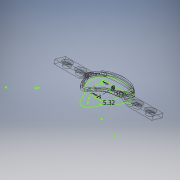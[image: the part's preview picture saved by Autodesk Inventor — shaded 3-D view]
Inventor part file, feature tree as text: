
AUTODESK INVENTOR PART (.ipt)
format: ipt  version: 2018 (Build 220112000, 112)  size: 2,541,568 bytes
history: native  units: mm
features: sketch x75, extrude x69, fillet x43, mirror x3, shell x1, hole x1
ambient origin geometry x8: Origin, YZ Plane, XZ Plane, XY Plane, X Axis, Y Axis, Z Axis, Center Point
bodies: Solid1 (feature_tree)
feature tree (192):
  extrude  "Extrusion1"  TaperAngle=0.0deg  [1 undecoded]
  extrude  "Extrusion2"  Depth=10.0mm
  extrude  "Extrusion3"  TaperAngle=0.0deg  [1 undecoded]
  shell  "Shell2"  Thickness=0.0mm
  extrude  "Extrusion4"  Depth=1.6mm
  extrude  "Extrusion6"  Depth=10.0mm TaperAngle=0.0deg
  extrude  "Extrusion7"  Depth=1.75mm
  extrude  "Extrusion8"  Depth=2.0mm
  extrude  "Extrusion9"  Depth=10.0mm TaperAngle=0.0deg
  extrude  "Extrusion11"  Depth=10.0mm TaperAngle=0.0deg
  fillet  "Fillet1"  Radius=10.0mm
  fillet  "Fillet2"  Radius=10.0mm
  fillet  "Fillet3"  [1 undecoded]
  fillet  "Fillet4"  Radius=0.541mm
  fillet  "Fillet5"  [1 undecoded]
  extrude  "Extrusion12"  Depth=7.5mm TaperAngle=0.0deg
  extrude  "Extrusion13"  TaperAngle=0.0deg  [1 undecoded]
  extrude  "Extrusion16"  Depth=51.0mm TaperAngle=0.0deg
  extrude  "Extrusion17"  TaperAngle=0.0deg  [1 undecoded]
  extrude  "Extrusion18"  Depth=10.0mm TaperAngle=0.0deg
  extrude  "Extrusion19"  Depth=10.0mm TaperAngle=0.0deg
  fillet  "Fillet6"  Radius=6.0mm
  extrude  "Extrusion20"  Depth=42.0mm TaperAngle=0.0deg
  fillet  "Fillet7"  Radius=42.0mm
  extrude  "Extrusion21"  Depth=2.6mm
  extrude  "Extrusion22"  Depth=2.6mm
  sketch  "Sketch23"  dims[d147=12.0125mm d148=12.0125mm]
  extrude  "Extrusion24"  Depth=12.0125mm
  extrude  "Extrusion26"  Depth=17.5mm
  extrude  "Extrusion28"  Depth=3.0mm
  extrude  "Extrusion32"  Depth=3.0mm
  extrude  "Extrusion37"  Depth=2.0mm TaperAngle=0.0deg
  extrude  "Extrusion38"  Depth=10.0mm TaperAngle=0.0deg
  extrude  "Extrusion40"  Depth=3.11mm
  extrude  "Extrusion41"  Depth=10.0mm TaperAngle=0.0deg
  extrude  "Extrusion42"  Depth=0.365mm TaperAngle=0.0deg
  extrude  "Extrusion43"  TaperAngle=0.0deg  [1 undecoded]
  extrude  "Extrusion44"  TaperAngle=0.0deg  [1 undecoded]
  hole  "Hole1"  [1 undecoded]
  sketch  "Sketch45"  dims[d203=20.0mm d204=15.65mm d205=0.0mm]
  extrude  "Extrusion45"  Depth=15.65mm TaperAngle=0.0deg
  extrude  "Extrusion47"  Depth=0.861mm
  mirror  "Mirror1"
  extrude  "Extrusion48"  Depth=1.61mm
  fillet  "Fillet23"  [1 undecoded]
  fillet  "Fillet24"  Radius=1.92mm
  extrude  "Extrusion49"  Depth=0.276mm
  extrude  "Extrusion50"  TaperAngle=0.0deg  [1 undecoded]
  extrude  "Extrusion54"  TaperAngle=0.0deg  [1 undecoded]
  extrude  "Extrusion55"  Depth=2.5mm
  extrude  "Extrusion56"  TaperAngle=0.0deg  [1 undecoded]
  extrude  "Extrusion57"  Depth=10.0mm TaperAngle=0.0deg
  sketch  "Sketch61"  dims[d255=2.57mm d256=2.37mm]
  extrude  "Extrusion58"  Depth=0.83mm TaperAngle=0.0deg
  extrude  "Extrusion59"  Depth=2.37mm
  extrude  "Extrusion60"  Depth=4.5mm
  fillet  "Fillet27"  Radius=0.83mm
  fillet  "Fillet28"  Radius=6.37mm
  extrude  "Extrusion61"  Depth=2.0mm TaperAngle=0.0deg
  fillet  "Fillet29"  Radius=6.71mm
  fillet  "Fillet30"  Radius=6.71mm
  fillet  "Fillet31"  [1 undecoded]
  fillet  "Fillet32"  Radius=2.0mm
  extrude  "Extrusion62"  Depth=2.0mm
  fillet  "Fillet33"  Radius=2.0mm
  fillet  "Fillet34"  Radius=2.0mm
  fillet  "Fillet35"  Radius=2.0mm
  fillet  "Fillet36"  Radius=2.0mm
  extrude  "Extrusion63"  Depth=1.9mm
  extrude  "Extrusion64"  Depth=0.616mm
  extrude  "Extrusion65"  Depth=2.0mm
  fillet  "Fillet37"  Radius=1.76mm
  fillet  "Fillet38"  [1 undecoded]
  extrude  "Extrusion69"  Depth=0.409mm
  extrude  "Extrusion70"  Depth=6.7mm TaperAngle=0.0deg
  extrude  "Extrusion71"  TaperAngle=0.0deg  [1 undecoded]
  extrude  "Extrusion72"  Depth=2.0mm
  extrude  "Extrusion73"  Depth=6.7mm TaperAngle=0.0deg
  extrude  "Extrusion74"  Depth=2.0mm
  fillet  "Fillet42"  Radius=5.47mm
  fillet  "Fillet43"  Radius=0.184mm
  extrude  "Extrusion75"  Depth=10.0mm TaperAngle=0.0deg
  extrude  "Extrusion76"  [1 undecoded]
  mirror  "Mirror2"
  extrude  "Extrusion77"  [1 undecoded]
  extrude  "Extrusion78"  [1 undecoded]
  extrude  "Extrusion79"  [1 undecoded]
  mirror  "Mirror3"
  extrude  "Extrusion80"  [1 undecoded]
  extrude  "Extrusion81"  [1 undecoded]
  fillet  "Fillet44"  [1 undecoded]
  fillet  "Fillet45"  [1 undecoded]
  fillet  "Fillet46"  [1 undecoded]
  fillet  "Fillet47"  [1 undecoded]
  fillet  "Fillet48"  [1 undecoded]
  fillet  "Fillet49"  [1 undecoded]
  fillet  "Fillet50"  [1 undecoded]
  sketch  "Sketch86"
  fillet  "Fillet51"  [1 undecoded]
  fillet  "Fillet52"  [1 undecoded]
  fillet  "Fillet53"  [1 undecoded]
  fillet  "Fillet54"  [1 undecoded]
  sketch  "Sketch87"
  extrude  "Extrusion82"  [1 undecoded]
  extrude  "Extrusion83"  [1 undecoded]
  extrude  "Extrusion84"  [1 undecoded]
  fillet  "Fillet55"  [1 undecoded]
  fillet  "Fillet56"  [1 undecoded]
  extrude  "Extrusion85"  [1 undecoded]
  extrude  "Extrusion86"  [1 undecoded]
  extrude  "Extrusion87"  [1 undecoded]
  fillet  "Fillet57"  [1 undecoded]
  fillet  "Fillet58"  [1 undecoded]
  extrude  "Extrusion88"  [1 undecoded]
  extrude  "Extrusion89"  [1 undecoded]
  fillet  "Fillet59"  [1 undecoded]
  fillet  "Fillet60"  [1 undecoded]
  fillet  "Fillet61"  [1 undecoded]
  fillet  "Fillet62"  [1 undecoded]
  extrude  "Extrusion90"  [1 undecoded]
  sketch  "Sketch97"
  extrude  "Extrusion91"  [1 undecoded]
  fillet  "Fillet63"  [1 undecoded]
  sketch  "Sketch1"  dims[d0=10.0mm d1=0.0mm d4=0.0mm d5=0.0mm]
  sketch  "Sketch2"  dims[d6=10.0mm d7=0.0mm d9=1.2mm]
  sketch  "Sketch3"  dims[d10=0.0mm d11=0.0mm d14=0.0mm d15=0.0mm d16=0.0mm d17=0.0mm]
  sketch  "Sketch4"  dims[d18=0.0mm d19=0.0mm d20=1.6mm]
  sketch  "Sketch6"  dims[d21=0.0mm d22=0.0mm d25=10.0mm d26=0.0mm]
  sketch  "Sketch7"  dims[d27=2.23mm d28=1.75mm]
  sketch  "Sketch8"  dims[d29=2.79mm d30=2.0mm]
  sketch  "Sketch9"  dims[d31=5.19mm d32=10.0mm d33=0.0mm]
  sketch  "Sketch11"  dims[d34=10.0mm d35=0.0mm d40=10.0mm d41=0.0mm d42=10.0mm d43=0.0mm d44=10.0mm d45=0.0mm d46=0.0mm d47=0.0mm d48=0.541mm d49=0.0mm d50=0.0mm]
  sketch  "Sketch12"  dims[d51=4.84mm d52=7.5mm d53=0.0mm]
  sketch  "Sketch13"  dims[d54=0.0mm d55=0.0mm d59=0.0mm d60=0.0mm]
  sketch  "Sketch16"  dims[d78=51.0mm d79=0.0mm d84=51.0mm d85=0.0mm]
  sketch  "Sketch17"  dims[d94=51.0mm d95=0.0mm d123=0.0mm d124=0.0mm]
  sketch  "Sketch18"  dims[d125=0.0mm d126=0.0mm d131=10.0mm d132=0.0mm]
  sketch  "Sketch19"  dims[d133=10.0mm d134=0.0mm d135=10.0mm d136=0.0mm d137=6.0mm]
  sketch  "Sketch20"  dims[d138=1.9mm d139=42.0mm d140=0.0mm d141=42.0mm d142=0.0mm]
  sketch  "Sketch21"  dims[d143=2.6mm d144=2.6mm]
  sketch  "Sketch22"  dims[d145=2.6mm d146=2.6mm]
  sketch  "Sketch24"  dims[d149=17.5mm d150=17.5mm]
  sketch  "Sketch26"  dims[d151=3.0mm d152=3.0mm]
  sketch  "Sketch28"  dims[d153=3.0mm d154=3.0mm]
  sketch  "Sketch32"  dims[d155=2.6mm d156=6.0mm d157=4.4mm d158=2.0mm d159=14.3117mm d160=8.0mm d161=20.594885mm d162=12.0mm d163=0.0mm]
  sketch  "Sketch37"  dims[d170=10.0mm d171=0.0mm d172=10.0mm d173=0.0mm]
  sketch  "Sketch38"  dims[d174=3.64mm d175=3.11mm]
  sketch  "Sketch40"  dims[d176=0.0mm d177=0.0mm d178=10.0mm d179=0.0mm]
  sketch  "Sketch41"  dims[d186=0.365mm d187=0.0mm d190=0.365mm d191=0.0mm]
  sketch  "Sketch42"  dims[d192=0.0mm d193=0.0mm d194=0.0mm d195=0.0mm]
  sketch  "Sketch43"  dims[d196=0.0mm d197=0.0mm d198=0.0mm d199=0.0mm]
  sketch  "Sketch44"  dims[d200=0.0mm d201=0.0mm d202=2.0mm]
  sketch  "Sketch46"  dims[d206=0.675mm d207=0.861mm]
  sketch  "Sketch48"  dims[d208=0.8mm d209=1.61mm d210=0.0mm d211=0.0mm d212=1.92mm]
  sketch  "Sketch49"  dims[d213=2.91mm d214=0.276mm]
  sketch  "Sketch50"  dims[d215=0.425mm d218=0.0mm d219=0.0mm]
  sketch  "Sketch51"  dims[d222=10.0mm d223=0.0mm d226=0.0mm d227=0.0mm]
  sketch  "Sketch55"  dims[d228=5.04mm d229=2.5mm]
  sketch  "Sketch57"  dims[d241=10.0mm d242=0.0mm d245=0.0mm d246=0.0mm]
  sketch  "Sketch59"  dims[d247=10.0mm d248=0.0mm d249=1.22mm d250=0.0mm]
  sketch  "Sketch60"  dims[d251=0.0mm d252=0.0mm d253=0.83mm d254=0.0mm]
  sketch  "Sketch62"  dims[d257=9.0mm d258=5.320111mm d259=8.0mm d260=4.5mm d261=0.83mm d262=0.0mm d263=6.37mm d264=0.0mm]
  sketch  "Sketch63"  dims[d265=6.37mm d266=0.0mm d267=6.37mm d268=0.0mm d269=6.71mm d270=0.0mm d271=6.71mm d272=0.0mm d273=0.0mm d274=0.0mm d275=2.0mm]
  sketch  "Sketch64"  dims[d276=0.789mm d277=2.0mm d278=2.0mm d279=2.0mm d280=2.0mm d281=2.0mm]
  sketch  "Sketch65"  dims[d282=9.0mm d283=5.320111mm d284=8.0mm d285=1.9mm]
  sketch  "Sketch66"  dims[d286=0.3mm d287=0.616mm]
  sketch  "Sketch67"  dims[d288=2.0mm d289=2.0mm d290=1.76mm d291=0.0mm d292=0.0mm d293=0.0mm]
  sketch  "Sketch68"  dims[d294=0.6mm d295=0.0mm d296=0.409mm]
  sketch  "Sketch69"  dims[d297=0.323mm d298=6.7mm d299=0.0mm]
  sketch  "Sketch73"  dims[d300=6.7mm d301=0.0mm d302=0.0mm d303=0.0mm]
  sketch  "Sketch74"  dims[d304=2.0mm d305=2.0mm]
  sketch  "Sketch75"  dims[d306=0.0mm d307=0.0mm d308=6.7mm d309=0.0mm]
  sketch  "Sketch76"  dims[d310=2.0mm d311=0.241mm d312=5.47mm d313=0.184mm]
  sketch  "Sketch77"  dims[d314=0.0mm d315=0.0mm d316=10.0mm d317=0.0mm]
  sketch  "Sketch78"  dims[d318=2.0mm]
  sketch  "Sketch79"
  sketch  "Sketch80"
  sketch  "Sketch81"
  sketch  "Sketch82"
  sketch  "Sketch83"
  sketch  "Sketch84"
  sketch  "Sketch85"
  sketch  "Sketch88"
  sketch  "Sketch89"
  sketch  "Sketch90"
  sketch  "Sketch91"
  sketch  "Sketch92"
  sketch  "Sketch93"
  sketch  "Sketch94"
  sketch  "Sketch95"
  sketch  "Sketch96"
  sketch  "Sketch98"
note: 52 required parameter values undecoded (feature->parameter linkage not recoverable at this tier; creation-order binding heuristic only, values carry confidence <= 0.55)
